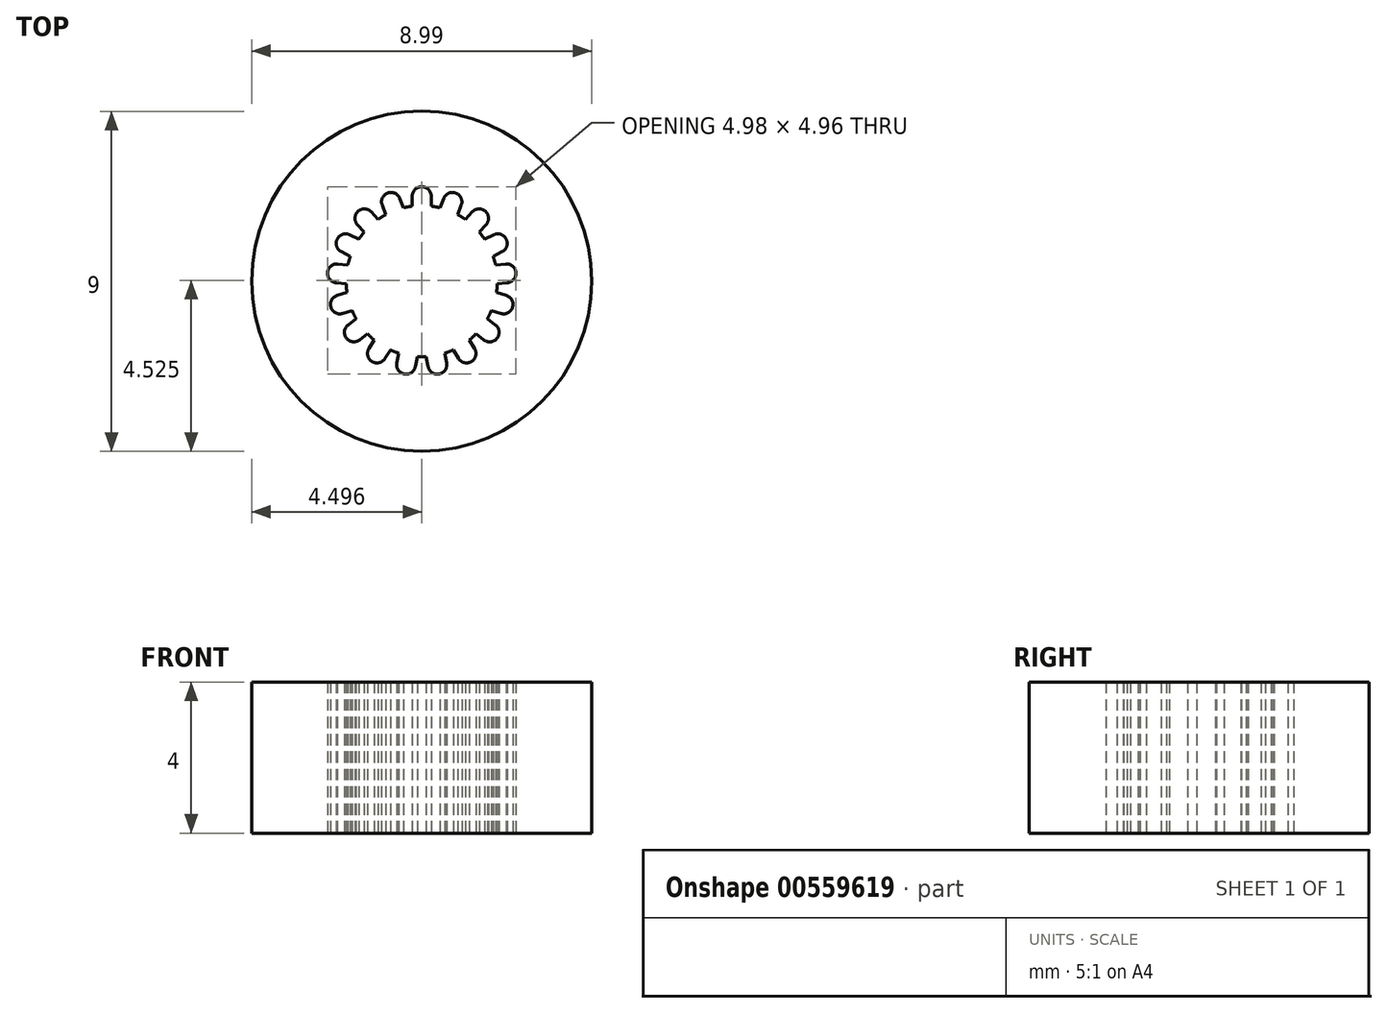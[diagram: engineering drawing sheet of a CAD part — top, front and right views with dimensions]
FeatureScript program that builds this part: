
annotation { "Feature Type Name" : "Feature", "Feature Type Description" : "" }
export const myFeature = defineFeature(function(context is Context, id is Id, definition is map)
    precondition{}
    {
        {
            var Q0;
            Q0=qCreatedBy(makeId("Top.planeOp"),FACE);
            var sketch = newSketch(context, id + "F0", { "sketchPlane" : qUnion([Q0])});
            skCircle(sketch, "E0", {"center": v(-0.01, -0.05) * mm, "radius": 2 * mm});
            skLineSegment(sketch, "E1", {"start": v(-2.01, -0.11) * mm, "end": v(-2.28, -0.09) * mm});
            skLineSegment(sketch, "E2", {"start": v(-1.97, 0.39) * mm, "end": v(-2.23, 0.41) * mm});
            skArc(sketch, "E3", {"start": v(-2.5, 0.18) * mm, "mid": v(-2.45, 0) * mm, "end": v(-2.28, -0.09) * mm});
            skArc(sketch, "E4", {"start": v(-2.23, 0.41) * mm, "mid": v(-2.41, 0.35) * mm, "end": v(-2.5, 0.18) * mm});
            skLineSegment(sketch, "E5", {"start": v(-2, -0.35) * mm, "end": v(-2.25, -0.42) * mm});
            skLineSegment(sketch, "E6", {"start": v(-1.85, -0.83) * mm, "end": v(-2.1, -0.9) * mm});
            skLineSegment(sketch, "E7", {"start": v(-1.75, -1.04) * mm, "end": v(-1.96, -1.2) * mm});
            skLineSegment(sketch, "E8", {"start": v(-1.45, -1.44) * mm, "end": v(-1.66, -1.6) * mm});
            skLineSegment(sketch, "E9", {"start": v(-1.27, -1.6) * mm, "end": v(-1.41, -1.83) * mm});
            skLineSegment(sketch, "E10", {"start": v(-0.85, -1.86) * mm, "end": v(-0.99, -2.1) * mm});
            skLineSegment(sketch, "E11", {"start": v(-0.62, -1.95) * mm, "end": v(-0.67, -2.21) * mm});
            skLineSegment(sketch, "E12", {"start": v(-0.13, -2.04) * mm, "end": v(-0.18, -2.3) * mm});
            skLineSegment(sketch, "E13", {"start": v(-1.9, 0.61) * mm, "end": v(-2.14, 0.73) * mm});
            skLineSegment(sketch, "E14", {"start": v(-1.68, 1.06) * mm, "end": v(-1.92, 1.18) * mm});
            skLineSegment(sketch, "E15", {"start": v(-1.54, 1.25) * mm, "end": v(-1.71, 1.45) * mm});
            skLineSegment(sketch, "E16", {"start": v(-1.17, 1.59) * mm, "end": v(-1.35, 1.79) * mm});
            skLineSegment(sketch, "E17", {"start": v(-0.96, 1.71) * mm, "end": v(-1.06, 1.96) * mm});
            skLineSegment(sketch, "E18", {"start": v(-0.5, 1.9) * mm, "end": v(-0.6, 2.14) * mm});
            skLineSegment(sketch, "E19", {"start": v(-0.26, 1.94) * mm, "end": v(-0.26, 2.2) * mm});
            skLineSegment(sketch, "E20", {"start": v(0.24, 1.94) * mm, "end": v(0.24, 2.2) * mm});
            skLineSegment(sketch, "E21", {"start": v(0.47, 1.9) * mm, "end": v(0.57, 2.14) * mm});
            skLineSegment(sketch, "E22", {"start": v(0.94, 1.71) * mm, "end": v(1.03, 1.96) * mm});
            skLineSegment(sketch, "E23", {"start": v(1.14, 1.59) * mm, "end": v(1.32, 1.79) * mm});
            skArc(sketch, "E24", {"start": v(-0.47, -2.5) * mm, "mid": v(-0.29, -2.46) * mm, "end": v(-0.18, -2.3) * mm});
            skArc(sketch, "E25", {"start": v(-0.67, -2.21) * mm, "mid": v(-0.63, -2.4) * mm, "end": v(-0.47, -2.5) * mm});
            skArc(sketch, "E26", {"start": v(-1.33, -2.17) * mm, "mid": v(-1.14, -2.2) * mm, "end": v(-0.99, -2.1) * mm});
            skArc(sketch, "E27", {"start": v(-1.41, -1.83) * mm, "mid": v(-1.44, -2.02) * mm, "end": v(-1.33, -2.17) * mm});
            skArc(sketch, "E28", {"start": v(-2.01, -1.55) * mm, "mid": v(-1.85, -1.65) * mm, "end": v(-1.66, -1.6) * mm});
            skArc(sketch, "E29", {"start": v(-1.96, -1.2) * mm, "mid": v(-2.06, -1.36) * mm, "end": v(-2.01, -1.55) * mm});
            skArc(sketch, "E30", {"start": v(-2.42, -0.73) * mm, "mid": v(-2.3, -0.88) * mm, "end": v(-2.1, -0.9) * mm});
            skArc(sketch, "E31", {"start": v(-2.25, -0.42) * mm, "mid": v(-2.4, -0.54) * mm, "end": v(-2.42, -0.73) * mm});
            skArc(sketch, "E32", {"start": v(-2.25, 1.07) * mm, "mid": v(-2.26, 0.88) * mm, "end": v(-2.14, 0.73) * mm});
            skPoint(sketch, "E32.startSnap0", {"position": v(-2.25, 1.07) * mm});
            skArc(sketch, "E33", {"start": v(-1.92, 1.18) * mm, "mid": v(-2.1, 1.2) * mm, "end": v(-2.25, 1.07) * mm});
            skArc(sketch, "E34", {"start": v(-1.71, 1.79) * mm, "mid": v(-1.78, 1.62) * mm, "end": v(-1.71, 1.45) * mm});
            skArc(sketch, "E35", {"start": v(-1.35, 1.79) * mm, "mid": v(-1.53, 1.87) * mm, "end": v(-1.71, 1.79) * mm});
            skArc(sketch, "E36", {"start": v(-0.92, 2.29) * mm, "mid": v(-1.06, 2.15) * mm, "end": v(-1.06, 1.96) * mm});
            skArc(sketch, "E37", {"start": v(-0.6, 2.14) * mm, "mid": v(-0.73, 2.28) * mm, "end": v(-0.92, 2.29) * mm});
            skArc(sketch, "E38", {"start": v(-0.01, 2.45) * mm, "mid": v(-0.2, 2.38) * mm, "end": v(-0.26, 2.2) * mm});
            skArc(sketch, "E39.MirrorCS", {"start": v(1.3, -2.17) * mm, "mid": v(1.11, -2.2) * mm, "end": v(0.96, -2.1) * mm});
            skArc(sketch, "E40.MirrorCS", {"start": v(1.32, 1.79) * mm, "mid": v(1.5, 1.87) * mm, "end": v(1.69, 1.79) * mm});
            skLineSegment(sketch, "E41.MirrorCS", {"start": v(1.72, -1.04) * mm, "end": v(1.93, -1.2) * mm});
            skArc(sketch, "E42.MirrorCS", {"start": v(1.69, 1.79) * mm, "mid": v(1.75, 1.62) * mm, "end": v(1.69, 1.45) * mm});
            skArc(sketch, "E43.MirrorCS", {"start": v(0.65, -2.21) * mm, "mid": v(0.6, -2.4) * mm, "end": v(0.45, -2.5) * mm});
            skArc(sketch, "E44.MirrorCS", {"start": v(1.38, -1.83) * mm, "mid": v(1.41, -2.02) * mm, "end": v(1.3, -2.17) * mm});
            skArc(sketch, "E45.MirrorCS", {"start": v(2.22, 1.07) * mm, "mid": v(2.24, 0.88) * mm, "end": v(2.11, 0.73) * mm});
            skArc(sketch, "E46.MirrorCS", {"start": v(0.89, 2.29) * mm, "mid": v(1.03, 2.15) * mm, "end": v(1.03, 1.96) * mm});
            skArc(sketch, "E47.MirrorCS", {"start": v(1.93, -1.2) * mm, "mid": v(2.03, -1.36) * mm, "end": v(1.98, -1.55) * mm});
            skArc(sketch, "E48.MirrorCS", {"start": v(2.48, 0.18) * mm, "mid": v(2.42, 0) * mm, "end": v(2.25, -0.09) * mm});
            skArc(sketch, "E49.MirrorCS", {"start": v(1.89, 1.18) * mm, "mid": v(2.08, 1.2) * mm, "end": v(2.22, 1.07) * mm});
            skArc(sketch, "E50.MirrorCS", {"start": v(0.45, -2.5) * mm, "mid": v(0.26, -2.46) * mm, "end": v(0.15, -2.3) * mm});
            skArc(sketch, "E51.MirrorCS", {"start": v(1.98, -1.55) * mm, "mid": v(1.82, -1.65) * mm, "end": v(1.63, -1.6) * mm});
            skArc(sketch, "E52.MirrorCS", {"start": v(2.22, -0.42) * mm, "mid": v(2.37, -0.54) * mm, "end": v(2.4, -0.73) * mm});
            skArc(sketch, "E53.MirrorCS", {"start": v(2.4, -0.73) * mm, "mid": v(2.27, -0.88) * mm, "end": v(2.08, -0.9) * mm});
            skLineSegment(sketch, "E54.MirrorCS", {"start": v(1.42, -1.44) * mm, "end": v(1.63, -1.6) * mm});
            skLineSegment(sketch, "E55.MirrorCS", {"start": v(1.24, -1.6) * mm, "end": v(1.38, -1.83) * mm});
            skLineSegment(sketch, "E56.MirrorCS", {"start": v(1.83, -0.83) * mm, "end": v(2.08, -0.9) * mm});
            skLineSegment(sketch, "E57.MirrorCS", {"start": v(0.82, -1.86) * mm, "end": v(0.96, -2.1) * mm});
            skLineSegment(sketch, "E58.MirrorCS", {"start": v(1.96, -0.35) * mm, "end": v(2.22, -0.42) * mm});
            skLineSegment(sketch, "E59.MirrorCS", {"start": v(0.6, -1.95) * mm, "end": v(0.65, -2.21) * mm});
            skLineSegment(sketch, "E60.MirrorCS", {"start": v(1.94, 0.39) * mm, "end": v(2.2, 0.41) * mm});
            skLineSegment(sketch, "E61.MirrorCS", {"start": v(0.1, -2.04) * mm, "end": v(0.15, -2.3) * mm});
            skLineSegment(sketch, "E62.MirrorCS", {"start": v(1.87, 0.61) * mm, "end": v(2.11, 0.73) * mm});
            skLineSegment(sketch, "E63.MirrorCS", {"start": v(1.65, 1.06) * mm, "end": v(1.89, 1.18) * mm});
            skLineSegment(sketch, "E64.MirrorCS", {"start": v(1.5, 1.25) * mm, "end": v(1.69, 1.45) * mm});
            skLineSegment(sketch, "E65.MirrorCS", {"start": v(1.98, -0.11) * mm, "end": v(2.25, -0.09) * mm});
            skArc(sketch, "E66.MirrorCS", {"start": v(-0.01, 2.45) * mm, "mid": v(0.16, 2.38) * mm, "end": v(0.24, 2.2) * mm});
            skArc(sketch, "E67.MirrorCS", {"start": v(2.2, 0.41) * mm, "mid": v(2.39, 0.35) * mm, "end": v(2.48, 0.18) * mm});
            skPoint(sketch, "E68.MirrorP", {"position": v(2.22, 1.07) * mm});
            skArc(sketch, "E69.MirrorCS", {"start": v(0.57, 2.14) * mm, "mid": v(0.7, 2.28) * mm, "end": v(0.89, 2.29) * mm});
            skCircle(sketch, "E70", {"center": v(-0.01, -0.05) * mm, "radius": 4.5 * mm});
            skSolve(sketch);
        }
        {
            var Q0;
            {var subQ8=sQuery(id+"F0.wireOp",EDGE,"E1");Q0=makeQuery(id+"F0.imprint","IMPRINT",FACE,{"disambiguationData":[TD([[makeQuery(id+"F0.imprint","IMPRINT",EDGE,{"derivedFrom":subQ8}),1.0]])]});}
            extrude(context, id + "F1", {"entities" : qUnion([Q0]), "depth" : 4 * mm, "offsetDistance" : 25 * mm});
        }
    });
